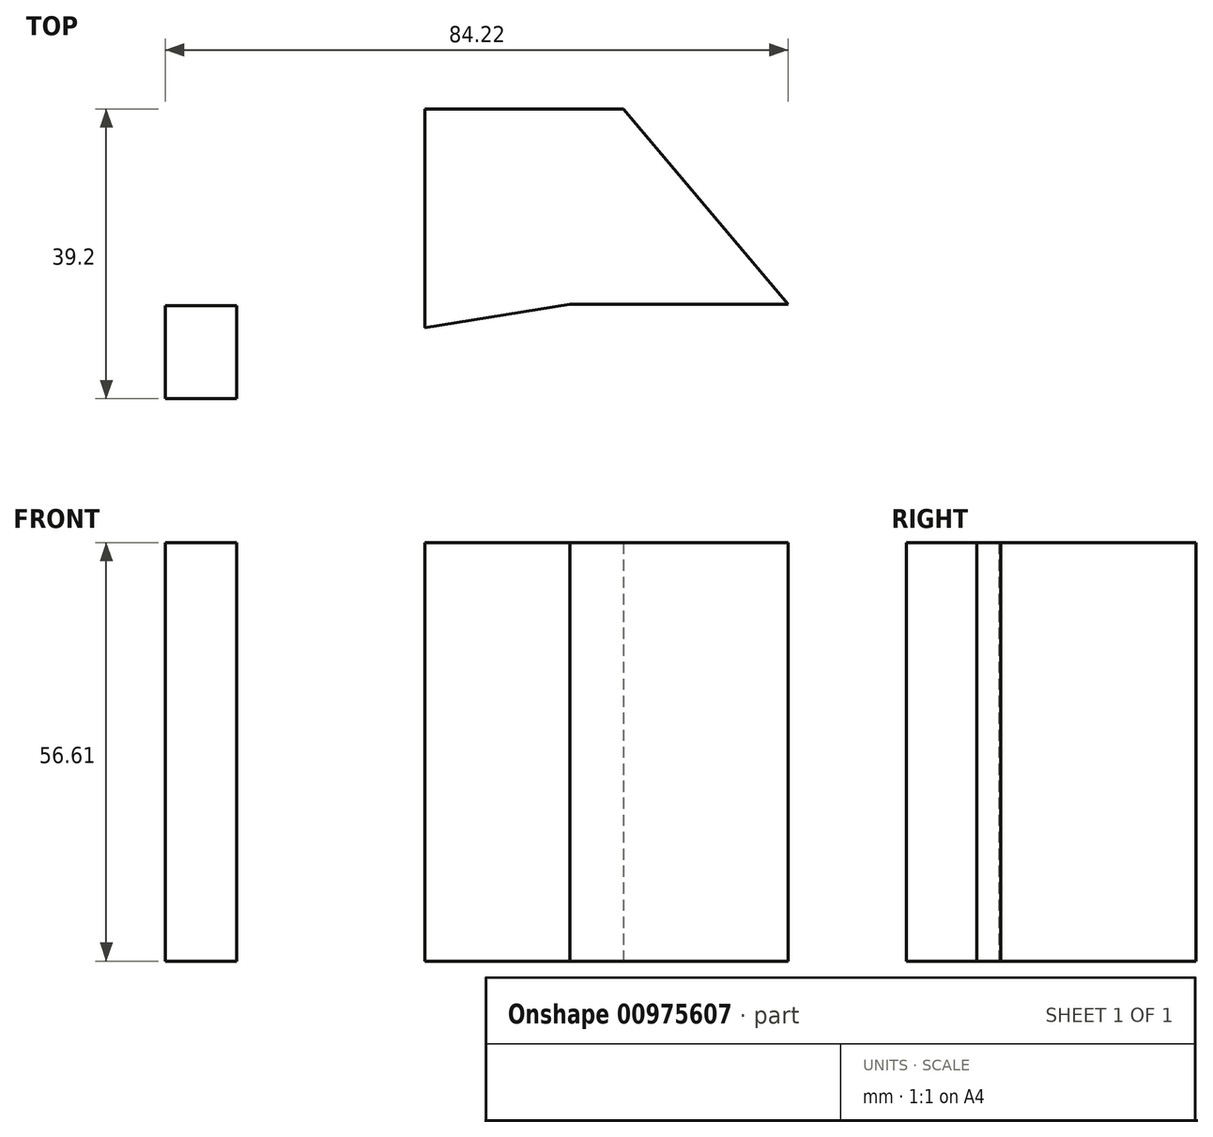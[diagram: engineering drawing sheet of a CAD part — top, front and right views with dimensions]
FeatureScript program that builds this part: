
annotation { "Feature Type Name" : "Feature", "Feature Type Description" : "" }
export const myFeature = defineFeature(function(context is Context, id is Id, definition is map)
    precondition{}
    {
        {
            var Q0;
            Q0=qCreatedBy(makeId("Top.planeOp"),FACE);
            var sketch = newSketch(context, id + "F0", { "sketchPlane" : qUnion([Q0])});
            skLineSegment(sketch, "E0", {"start": v(26.84, 67.47) * mm, "end": v(0, 67.47) * mm});
            skLineSegment(sketch, "E1", {"start": v(0, 67.47) * mm, "end": v(26.84, 67.47) * mm});
            skLineSegment(sketch, "E2", {"start": v(49.11, 41.03) * mm, "end": v(26.84, 67.47) * mm});
            skLineSegment(sketch, "E3", {"start": v(86.7, 41.03) * mm, "end": v(49.11, 41.03) * mm});
            skLineSegment(sketch, "E4", {"start": v(0, 37.83) * mm, "end": v(0, 67.47) * mm});
            skLineSegment(sketch, "E5", {"start": v(19.63, 41.03) * mm, "end": v(0, 37.83) * mm});
            skLineSegment(sketch, "E6", {"start": v(49.11, 41.03) * mm, "end": v(19.63, 41.03) * mm});
            skLineSegment(sketch, "E7", {"start": v(-6.75, 180.25) * mm, "end": v(46.46, 124.7) * mm});
            skLineSegment(sketch, "E8.bottom", {"start": v(-25.45, 28.27) * mm, "end": v(-35.11, 28.27) * mm});
            skLineSegment(sketch, "E8.top", {"start": v(-25.45, 40.82) * mm, "end": v(-35.11, 40.82) * mm});
            skLineSegment(sketch, "E8.left", {"start": v(-25.45, 28.27) * mm, "end": v(-25.45, 40.82) * mm});
            skLineSegment(sketch, "E8.right", {"start": v(-35.11, 28.27) * mm, "end": v(-35.11, 40.82) * mm});
            skSolve(sketch);
        }
        {
            var Q0;
            Q0 = qSketchRegion(id + "F0", true);
            extrude(context, id + "F1", {"entities" : qUnion([Q0]), "depth" : 56.6 * mm, "offsetDistance" : 25.4 * mm});
        }
    });
